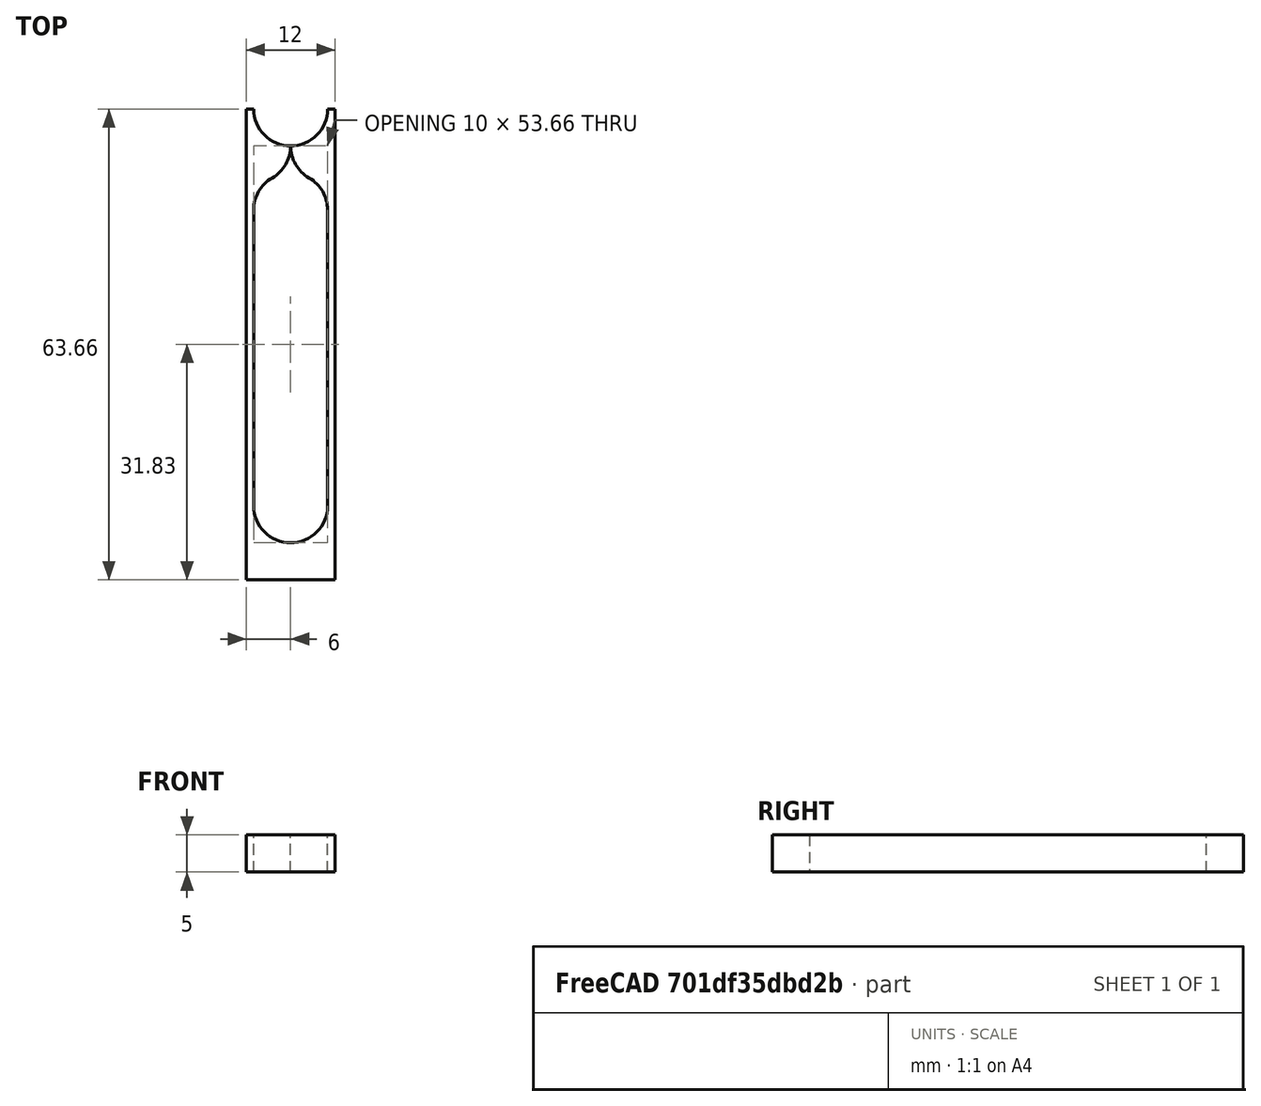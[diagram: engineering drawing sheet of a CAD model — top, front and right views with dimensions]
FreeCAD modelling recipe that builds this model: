
FCSTD DOCUMENT  (FreeCAD 0.18R)
Label: thread-release-clip
License: All rights reserved
LicenseURL: http://en.wikipedia.org/wiki/All_rights_reserved
objects: Sketcher::SketchObject×1, PartDesign::Pad×1, PartDesign::Body×1
note: 4 computed .brp shape members not serialized (recipe doc carries the construction recipe); baked Part::Feature solids carry a one-line shape summary decoded from their .brp

FEATURE [Sketcher::SketchObject] Sketch
  MapMode = 5
  Support = -> [XY_Plane]
  sketch-geometry (19):
    g0: ArcOfCircle CenterX=0 CenterY=13.6603 CenterZ=0 NormalX=0 NormalY=0 NormalZ=1 AngleXU=0 Radius=5 StartAngle=3.14159 EndAngle=4.71239
    g1: ArcOfCircle CenterX=-5 CenterY=8.66025 CenterZ=0 NormalX=0 NormalY=0 NormalZ=1 AngleXU=0 Radius=5 StartAngle=5.23599 EndAngle=6.28319
    g2: ArcOfCircle CenterX=-4e-16 CenterY=-4.42589e-08 CenterZ=0 NormalX=0 NormalY=0 NormalZ=1 AngleXU=0 Radius=5 StartAngle=2.0944 EndAngle=3.14159
    g3: LineSegment StartX=-5 StartY=0 StartZ=0 EndX=-5 EndY=-40 EndZ=0
    g4: ArcOfCircle CenterX=0 CenterY=-40 CenterZ=0 NormalX=0 NormalY=0 NormalZ=1 AngleXU=0 Radius=5 StartAngle=3.14159 EndAngle=6.28319
    g5: LineSegment StartX=5 StartY=-40 StartZ=0 EndX=5 EndY=0 EndZ=0
    g6: ArcOfCircle CenterX=3e-16 CenterY=-4.42589e-08 CenterZ=0 NormalX=0 NormalY=0 NormalZ=1 AngleXU=0 Radius=5 StartAngle=8.85177e-09 EndAngle=1.0472
    g7: ArcOfCircle CenterX=5 CenterY=8.66025 CenterZ=0 NormalX=0 NormalY=0 NormalZ=1 AngleXU=0 Radius=5 StartAngle=3.14159 EndAngle=4.18879
    g8: ArcOfCircle CenterX=0 CenterY=13.6603 CenterZ=0 NormalX=0 NormalY=0 NormalZ=1 AngleXU=0 Radius=5 StartAngle=4.71239 EndAngle=6.28319
    g9: LineSegment StartX=5 StartY=13.6603 StartZ=0 EndX=6 EndY=13.6603 EndZ=0
    g10: LineSegment StartX=6 StartY=13.6603 StartZ=0 EndX=6 EndY=-50 EndZ=0
    g11: LineSegment StartX=6 StartY=-50 StartZ=0 EndX=-6 EndY=-50 EndZ=0
    g12: LineSegment StartX=-6 StartY=-50 StartZ=0 EndX=-6 EndY=13.6603 EndZ=0
    g13: LineSegment StartX=-6 StartY=13.6603 StartZ=0 EndX=-5 EndY=13.6603 EndZ=0
    g14: LineSegment [constr] StartX=0 StartY=13.6603 StartZ=0 EndX=0 EndY=-40 EndZ=0
    g15: LineSegment [constr] StartX=-5 StartY=0 StartZ=0 EndX=-2.5 EndY=4.33013 EndZ=0
    g16: LineSegment [constr] StartX=-2.5 StartY=4.33013 StartZ=0 EndX=-9e-16 EndY=8.66025 EndZ=0
    g17: LineSegment [constr] StartX=-9e-16 StartY=8.66025 StartZ=0 EndX=2.5 EndY=4.33013 EndZ=0
    g18: LineSegment [constr] StartX=2.5 StartY=4.33013 StartZ=0 EndX=5 EndY=0 EndZ=0
  constraints (58):
    c: Vertical(g3)
    c: Vertical(g5)
    c: Coincident(g9,g10)
    c: Vertical(g10)
    c: Coincident(g10,g11)
    c: Horizontal(g11)
    c: Coincident(g11,g12)
    c: Vertical(g12)
    c: Coincident(g12,g13)
    c: Coincident(g13,g0)
    c: Coincident(g0,g1)
    c: Coincident(g1,g2)
    c: Coincident(g2,g3)
    c: Coincident(g4,g3)
    c: Coincident(g4,g5)
    c: Coincident(g5,g6)
    c: Coincident(g7,g6)
    c: Coincident(g8,g9)
    c: Horizontal(g13)
    c: Horizontal(g9)
    c: Equal(g9,g13)
    c: Equal(g12,g10)
    c: Equal(g3,g5)
    c: DistanceX(g13,g13) = 1
    c: Vertical(g14)
    c: Tangent(g14,g1)
    c: PointOnObject(g14,g-2)
    c: Coincident(g0,g14)
    c: Coincident(g8,g0)
    c: Angle(g0) = 1.5708
    c: Radius(g1) = 5
    c: Radius(g7) = 5
    c: Radius(g2) = 5
    c: Radius(g6) = 5
    c: DistanceX(g11,g3) = 1
    c: Angle(g4) = 3.14159
    c: PointOnObject(g2,g-1)
    c: PointOnObject(g5,g-1)
    c: Radius(g0) = 5
    c: Coincident(g15,g16)
    c: Coincident(g16,g17)
    c: Coincident(g17,g18)
    c: Coincident(g15,g2)
    c: Coincident(g1,g15)
    c: Coincident(g16,g0)
    c: Coincident(g17,g6)
    c: Coincident(g18,g5)
    c: Equal(g16,g15)
    c: Equal(g17,g18)
    c: Equal(g16,g15)
    c: Parallel(g16,g15)
    c: Parallel(g17,g18)
    c: Coincident(g0,g7)
    c: Coincident(g14,g4)
    c: PointOnObject(g0,g14)
    c: DistanceY(g4,g2) = 40
    c: DistanceY(g10,g4) = 10
    c: Coincident(g0,g8)
FEATURE [PartDesign::Pad] Pad
  Length = 5
  Length2 = 100
  Profile = -> Sketch
  Type = 0
FEATURE [PartDesign::Body] Body
  Group = -> [Sketch,Pad]
  Origin = -> Origin
  Tip = -> Pad
